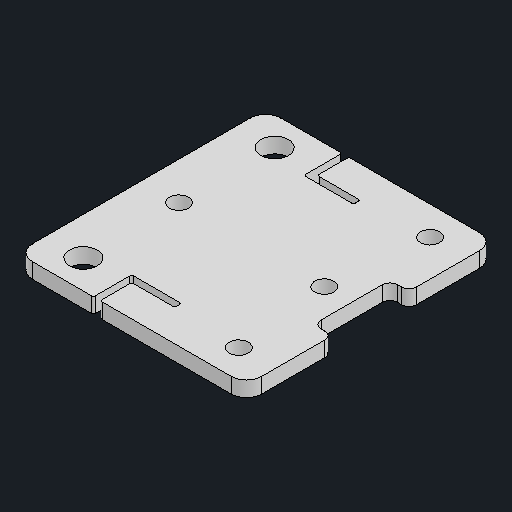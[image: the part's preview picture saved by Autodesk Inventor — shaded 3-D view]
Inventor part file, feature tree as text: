
AUTODESK INVENTOR PART (.ipt)
format: ipt  version: 2024.2 (Build 282272000, 272)  size: 114,176 bytes
history: native  units: mm
features: other x1, fillet x1
ambient origin geometry x8: Origin, YZ Plane, XZ Plane, XY Plane, X Axis, Y Axis, Z Axis, Center Point
bodies: Body1 (feature_tree)
feature tree (2):
  other  "솔리드1"
  fillet  "Fillet4"  [1 undecoded]
note: 1 required parameter value undecoded (feature->parameter linkage not recoverable at this tier; creation-order binding heuristic only, values carry confidence <= 0.55)
